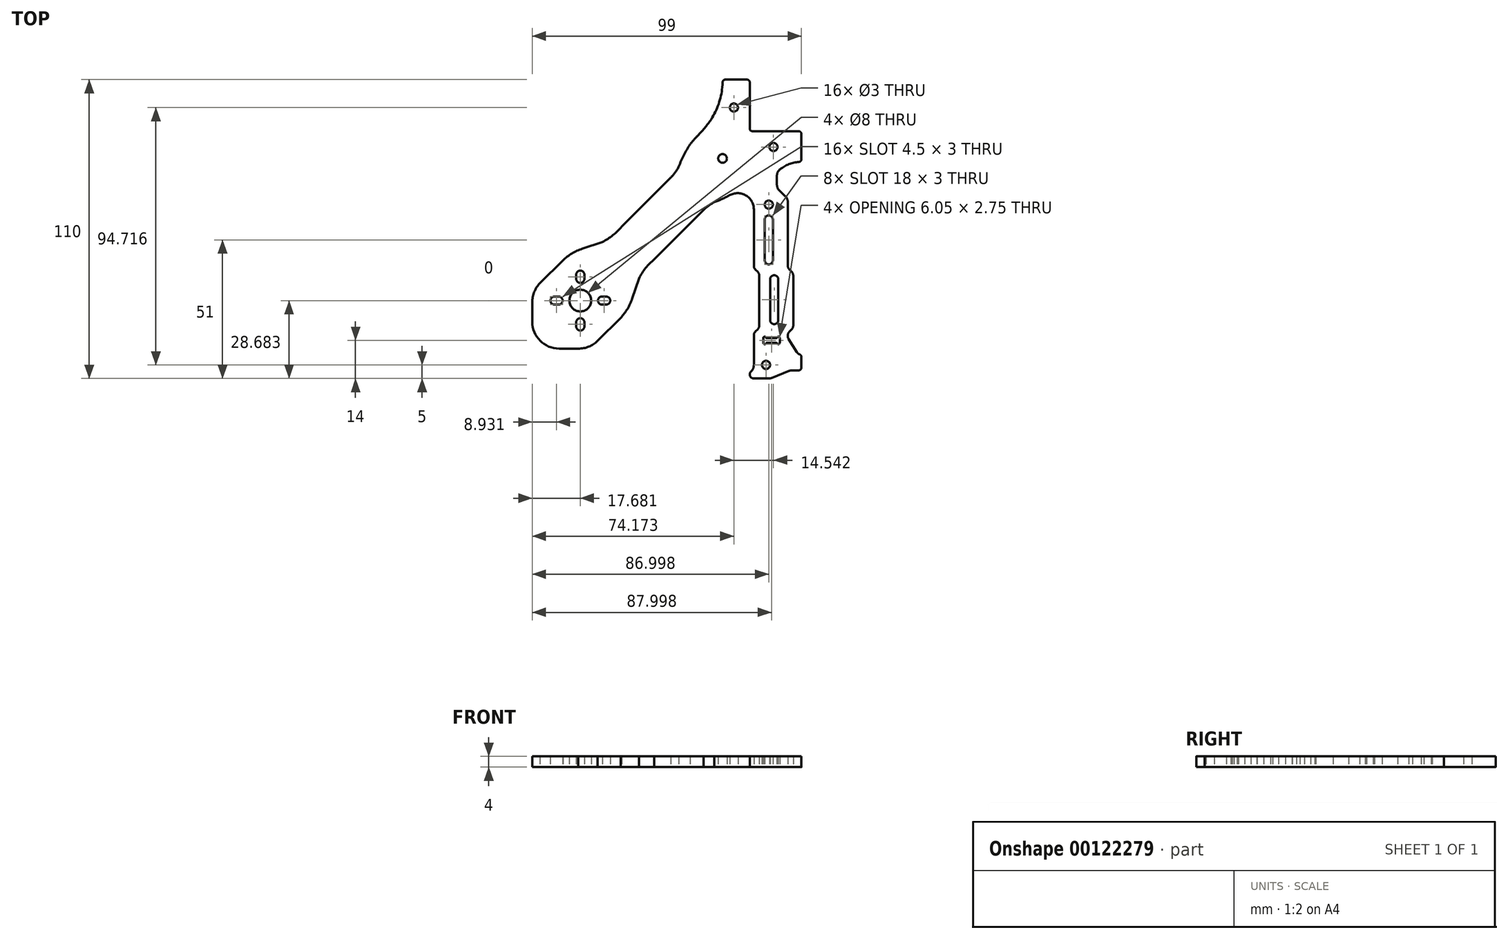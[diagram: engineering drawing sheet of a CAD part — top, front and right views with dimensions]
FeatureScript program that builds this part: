
annotation { "Feature Type Name" : "Feature", "Feature Type Description" : "" }
export const myFeature = defineFeature(function(context is Context, id is Id, definition is map)
    precondition{}
    {
        {
            var Q0;
            Q0=qCreatedBy(makeId("Top.planeOp"),FACE);
            var sketch = newSketch(context, id + "F0", { "sketchPlane" : qUnion([Q0])});
            skLineSegment(sketch, "E0", {"start": v(32, -55) * mm, "end": v(37.42, -55) * mm});
            skArc(sketch, "E1", {"start": v(31, -52.38) * mm, "mid": v(30.6, -54.04) * mm, "end": v(32, -55) * mm});
            skLineSegment(sketch, "E2", {"start": v(44.96, -52.21) * mm, "end": v(38.53, -54.79) * mm});
            skArc(sketch, "E3", {"start": v(31, -52.38) * mm, "mid": v(31.74, -51.37) * mm, "end": v(32, -50.15) * mm});
            skArc(sketch, "E4", {"start": v(37.42, -55) * mm, "mid": v(37.99, -54.95) * mm, "end": v(38.53, -54.79) * mm});
            skArc(sketch, "E5", {"start": v(46.08, -52) * mm, "mid": v(45.5, -52.05) * mm, "end": v(44.96, -52.21) * mm});
            skCircle(sketch, "E6", {"center": v(37.5, 9) * mm, "radius": 1.5 * mm});
            skLineSegment(sketch, "E7", {"start": v(46.08, -52) * mm, "end": v(48.5, -52) * mm});
            skArc(sketch, "E8", {"start": v(48.5, -52) * mm, "mid": v(49.2, -51.7) * mm, "end": v(49.5, -51) * mm});
            skLineSegment(sketch, "E9", {"start": v(33.41, -15.73) * mm, "end": v(32.58, -14.9) * mm});
            skLineSegment(sketch, "E10", {"start": v(32.58, -37.73) * mm, "end": v(33.41, -36.9) * mm});
            skLineSegment(sketch, "E11", {"start": v(32, -39.15) * mm, "end": v(32, -50.15) * mm});
            skLineSegment(sketch, "E12", {"start": v(34, -17.15) * mm, "end": v(34, -35.49) * mm});
            skArc(sketch, "E13", {"start": v(32.58, -37.73) * mm, "mid": v(32.15, -38.38) * mm, "end": v(32, -39.15) * mm});
            skArc(sketch, "E14", {"start": v(33.41, -36.9) * mm, "mid": v(33.85, -36.25) * mm, "end": v(34, -35.49) * mm});
            skArc(sketch, "E15", {"start": v(32, -13.49) * mm, "mid": v(32.15, -14.25) * mm, "end": v(32.58, -14.9) * mm});
            skArc(sketch, "E16", {"start": v(34, -17.15) * mm, "mid": v(33.85, -16.38) * mm, "end": v(33.41, -15.73) * mm});
            skCircle(sketch, "E17", {"center": v(-31.82, -26.32) * mm, "radius": 4 * mm});
            skArc(sketch, "E18", {"start": v(-41.32, -24.82) * mm, "mid": v(-42.82, -26.32) * mm, "end": v(-41.32, -27.82) * mm});
            skArc(sketch, "E19", {"start": v(-39.82, -27.82) * mm, "mid": v(-38.32, -26.32) * mm, "end": v(-39.82, -24.82) * mm});
            skArc(sketch, "E20", {"start": v(-30.32, -16.82) * mm, "mid": v(-31.82, -15.32) * mm, "end": v(-33.32, -16.82) * mm});
            skArc(sketch, "E21", {"start": v(-33.32, -18.32) * mm, "mid": v(-31.82, -19.82) * mm, "end": v(-30.32, -18.32) * mm});
            skArc(sketch, "E22", {"start": v(-23.82, -24.82) * mm, "mid": v(-25.32, -26.32) * mm, "end": v(-23.82, -27.82) * mm});
            skArc(sketch, "E23", {"start": v(-22.32, -27.82) * mm, "mid": v(-20.82, -26.32) * mm, "end": v(-22.32, -24.82) * mm});
            skArc(sketch, "E24", {"start": v(-30.32, -34.32) * mm, "mid": v(-31.82, -32.82) * mm, "end": v(-33.32, -34.32) * mm});
            skArc(sketch, "E25", {"start": v(-33.32, -35.82) * mm, "mid": v(-31.82, -37.32) * mm, "end": v(-30.32, -35.82) * mm});
            skLineSegment(sketch, "E26", {"start": v(-41.32, -24.82) * mm, "end": v(-39.82, -24.82) * mm});
            skLineSegment(sketch, "E27", {"start": v(-39.82, -27.82) * mm, "end": v(-41.32, -27.82) * mm});
            skLineSegment(sketch, "E28", {"start": v(-33.32, -16.82) * mm, "end": v(-33.32, -18.32) * mm});
            skLineSegment(sketch, "E29", {"start": v(-30.32, -16.82) * mm, "end": v(-30.32, -18.32) * mm});
            skLineSegment(sketch, "E30", {"start": v(-22.32, -24.82) * mm, "end": v(-23.82, -24.82) * mm});
            skLineSegment(sketch, "E31", {"start": v(-22.32, -27.82) * mm, "end": v(-23.82, -27.82) * mm});
            skLineSegment(sketch, "E32", {"start": v(-30.32, -34.32) * mm, "end": v(-30.32, -35.82) * mm});
            skLineSegment(sketch, "E33", {"start": v(-33.32, -34.32) * mm, "end": v(-33.32, -35.82) * mm});
            skLineSegment(sketch, "E34", {"start": v(-25.46, -41.17) * mm, "end": v(-16.97, -32.68) * mm});
            skLineSegment(sketch, "E35", {"start": v(-38.18, -11.47) * mm, "end": v(-46.67, -19.95) * mm});
            skArc(sketch, "E36", {"start": v(-49.5, -34.1) * mm, "mid": v(-46.6, -41.1) * mm, "end": v(-39.6, -44) * mm});
            skLineSegment(sketch, "E37", {"start": v(-49.5, -34.1) * mm, "end": v(-49.5, -27.02) * mm});
            skLineSegment(sketch, "E38", {"start": v(-39.6, -44) * mm, "end": v(-32.53, -44) * mm});
            skLineSegment(sketch, "E39", {"start": v(-12.73, -25.61) * mm, "end": v(-10.25, -18.19) * mm});
            skLineSegment(sketch, "E40", {"start": v(-31.11, -7.23) * mm, "end": v(-23.69, -4.75) * mm});
            skArc(sketch, "E41", {"start": v(-23.69, -4.75) * mm, "mid": v(-19.85, -2.3) * mm, "end": v(-16.62, 0.9) * mm});
            skArc(sketch, "E42", {"start": v(-4.6, -11.11) * mm, "mid": v(-7.8, -14.35) * mm, "end": v(-10.25, -18.19) * mm});
            skArc(sketch, "E43", {"start": v(-16.97, -32.68) * mm, "mid": v(-14.48, -29.37) * mm, "end": v(-12.73, -25.61) * mm});
            skArc(sketch, "E44", {"start": v(-31.11, -7.23) * mm, "mid": v(-34.87, -8.98) * mm, "end": v(-38.18, -11.47) * mm});
            skArc(sketch, "E45", {"start": v(-46.67, -19.95) * mm, "mid": v(-48.79, -23.2) * mm, "end": v(-49.5, -27.02) * mm});
            skArc(sketch, "E46", {"start": v(-32.53, -44) * mm, "mid": v(-28.7, -43.28) * mm, "end": v(-25.46, -41.17) * mm});
            skLineSegment(sketch, "E47", {"start": v(1.41, 18.94) * mm, "end": v(-16.62, 0.9) * mm});
            skLineSegment(sketch, "E48", {"start": v(32, 7.22) * mm, "end": v(32, -13.49) * mm});
            skArc(sketch, "E49", {"start": v(17.5, 9.92) * mm, "mid": v(15.37, 8.64) * mm, "end": v(13.5, 7) * mm});
            skArc(sketch, "E50", {"start": v(1.41, 18.94) * mm, "mid": v(3.1, 20.84) * mm, "end": v(4.42, 23) * mm});
            skLineSegment(sketch, "E51", {"start": v(46.5, -17.15) * mm, "end": v(46.5, -35.49) * mm});
            skLineSegment(sketch, "E52", {"start": v(45.08, -37.73) * mm, "end": v(45.91, -36.9) * mm});
            skLineSegment(sketch, "E53", {"start": v(45.91, -15.73) * mm, "end": v(45.08, -14.9) * mm});
            skLineSegment(sketch, "E54", {"start": v(44.5, -13.49) * mm, "end": v(44.5, 9.96) * mm});
            skLineSegment(sketch, "E55", {"start": v(44.5, -39.43) * mm, "end": v(44.5, -39.15) * mm});
            skArc(sketch, "E56", {"start": v(44.5, -13.49) * mm, "mid": v(44.65, -14.25) * mm, "end": v(45.08, -14.9) * mm});
            skArc(sketch, "E57", {"start": v(46.5, -17.15) * mm, "mid": v(46.35, -16.38) * mm, "end": v(45.91, -15.73) * mm});
            skArc(sketch, "E58", {"start": v(45.08, -37.73) * mm, "mid": v(44.65, -38.38) * mm, "end": v(44.5, -39.15) * mm});
            skArc(sketch, "E59", {"start": v(45.91, -36.9) * mm, "mid": v(46.35, -36.25) * mm, "end": v(46.5, -35.49) * mm});
            skLineSegment(sketch, "E60", {"start": v(41, -33.5) * mm, "end": v(41, -18.5) * mm});
            skLineSegment(sketch, "E61", {"start": v(38, -18.5) * mm, "end": v(38, -33.5) * mm});
            skArc(sketch, "E62", {"start": v(38, -33.5) * mm, "mid": v(39.5, -35) * mm, "end": v(41, -33.5) * mm});
            skArc(sketch, "E63", {"start": v(41, -18.5) * mm, "mid": v(39.5, -17) * mm, "end": v(38, -18.5) * mm});
            skLineSegment(sketch, "E64", {"start": v(39, -11.5) * mm, "end": v(39, 3.5) * mm});
            skLineSegment(sketch, "E65", {"start": v(36, 3.5) * mm, "end": v(36, -11.5) * mm});
            skArc(sketch, "E66", {"start": v(36, -11.5) * mm, "mid": v(37.5, -13) * mm, "end": v(39, -11.5) * mm});
            skArc(sketch, "E67", {"start": v(39, 3.5) * mm, "mid": v(37.5, 5) * mm, "end": v(36, 3.5) * mm});
            skCircle(sketch, "E68", {"center": v(39.22, 30.17) * mm, "radius": 1.5 * mm});
            skCircle(sketch, "E69", {"center": v(24.67, 44.72) * mm, "radius": 1.5 * mm});
            skLineSegment(sketch, "E70", {"start": v(44.8, -40.49) * mm, "end": v(47.8, -45.29) * mm});
            skArc(sketch, "E71", {"start": v(44.5, -39.43) * mm, "mid": v(44.58, -39.98) * mm, "end": v(44.8, -40.49) * mm});
            skLineSegment(sketch, "E72", {"start": v(49.5, -47.05) * mm, "end": v(49.5, -51) * mm});
            skArc(sketch, "E73", {"start": v(47.8, -45.29) * mm, "mid": v(48.25, -45.79) * mm, "end": v(48.83, -46.11) * mm});
            skArc(sketch, "E74", {"start": v(49.5, -47.05) * mm, "mid": v(49.31, -46.48) * mm, "end": v(48.83, -46.11) * mm});
            skLineSegment(sketch, "E75", {"start": v(-4.6, -11.11) * mm, "end": v(13.5, 7) * mm});
            skArc(sketch, "E76", {"start": v(30.5, 37) * mm, "mid": v(30.8, 36.3) * mm, "end": v(31.5, 36) * mm});
            skLineSegment(sketch, "E77", {"start": v(31.5, 36) * mm, "end": v(48.5, 36) * mm});
            skArc(sketch, "E78", {"start": v(49.5, 35) * mm, "mid": v(49.2, 35.7) * mm, "end": v(48.5, 36) * mm});
            skLineSegment(sketch, "E79", {"start": v(30.5, 54) * mm, "end": v(30.5, 37) * mm});
            skArc(sketch, "E80", {"start": v(30.5, 54) * mm, "mid": v(30.2, 54.7) * mm, "end": v(29.5, 55) * mm});
            skCircle(sketch, "E81", {"center": v(36.5, -50) * mm, "radius": 1.5 * mm});
            skCircle(sketch, "E82", {"center": v(20.5, 26) * mm, "radius": 1.6 * mm});
            skArc(sketch, "E83", {"start": v(16.27, 40.35) * mm, "mid": v(19.05, 46) * mm, "end": v(20.4, 52.17) * mm});
            skArc(sketch, "E84", {"start": v(11.73, 34.76) * mm, "mid": v(14.15, 37.44) * mm, "end": v(16.27, 40.35) * mm});
            skArc(sketch, "E85", {"start": v(11.73, 34.76) * mm, "mid": v(10.12, 33.04) * mm, "end": v(8.61, 31.23) * mm});
            skArc(sketch, "E86", {"start": v(8.61, 31.23) * mm, "mid": v(6.25, 27.25) * mm, "end": v(4.42, 23) * mm});
            skArc(sketch, "E87", {"start": v(17.5, 9.92) * mm, "mid": v(20.33, 11.06) * mm, "end": v(23.05, 12.45) * mm});
            skArc(sketch, "E88", {"start": v(20.4, 52.17) * mm, "mid": v(20.47, 53.1) * mm, "end": v(20.51, 54.03) * mm});
            skArc(sketch, "E89", {"start": v(21.51, 55) * mm, "mid": v(20.82, 54.72) * mm, "end": v(20.51, 54.03) * mm});
            skLineSegment(sketch, "E90", {"start": v(21.51, 55) * mm, "end": v(29.5, 55) * mm});
            skLineSegment(sketch, "E91", {"start": v(40.5, 19.66) * mm, "end": v(40.5, 16.3) * mm});
            skLineSegment(sketch, "E92", {"start": v(41.45, 14.11) * mm, "end": v(43.54, 12.16) * mm});
            skArc(sketch, "E93", {"start": v(48.57, 24.7) * mm, "mid": v(44.9, 23.87) * mm, "end": v(41.65, 22.02) * mm});
            skArc(sketch, "E94", {"start": v(48.57, 24.7) * mm, "mid": v(49.23, 25.01) * mm, "end": v(49.5, 25.7) * mm});
            skLineSegment(sketch, "E95", {"start": v(49.5, 35) * mm, "end": v(49.5, 25.7) * mm});
            skArc(sketch, "E96", {"start": v(44.5, 9.96) * mm, "mid": v(44.25, 11.16) * mm, "end": v(43.54, 12.16) * mm});
            skArc(sketch, "E97", {"start": v(40.5, 16.3) * mm, "mid": v(40.75, 15.1) * mm, "end": v(41.45, 14.11) * mm});
            skArc(sketch, "E98", {"start": v(41.65, 22.02) * mm, "mid": v(40.8, 20.97) * mm, "end": v(40.5, 19.66) * mm});
            skArc(sketch, "E99", {"start": v(32, 7.22) * mm, "mid": v(29.03, 12.4) * mm, "end": v(23.05, 12.45) * mm});
            skLineSegment(sketch, "E100", {"start": v(41.52, -41.88) * mm, "end": v(41.52, -40.12) * mm});
            skLineSegment(sketch, "E101", {"start": v(35.47, -40.12) * mm, "end": v(35.47, -41.88) * mm});
            skArc(sketch, "E102", {"start": v(36.4, -39.88) * mm, "mid": v(35.84, -39.64) * mm, "end": v(35.47, -40.12) * mm});
            skArc(sketch, "E103", {"start": v(35.47, -41.88) * mm, "mid": v(35.84, -42.36) * mm, "end": v(36.4, -42.12) * mm});
            skArc(sketch, "E104", {"start": v(40.59, -42.12) * mm, "mid": v(41.15, -42.36) * mm, "end": v(41.52, -41.88) * mm});
            skArc(sketch, "E105", {"start": v(41.52, -40.12) * mm, "mid": v(41.15, -39.64) * mm, "end": v(40.59, -39.88) * mm});
            skLineSegment(sketch, "E106", {"start": v(36.84, -40.12) * mm, "end": v(40.16, -40.12) * mm});
            skLineSegment(sketch, "E107", {"start": v(40.16, -41.88) * mm, "end": v(36.84, -41.88) * mm});
            skArc(sketch, "E108", {"start": v(36.4, -39.88) * mm, "mid": v(36.59, -40.06) * mm, "end": v(36.84, -40.12) * mm});
            skArc(sketch, "E109", {"start": v(40.16, -40.12) * mm, "mid": v(40.4, -40.06) * mm, "end": v(40.59, -39.88) * mm});
            skArc(sketch, "E110", {"start": v(40.59, -42.12) * mm, "mid": v(40.4, -41.94) * mm, "end": v(40.16, -41.88) * mm});
            skArc(sketch, "E111", {"start": v(36.84, -41.88) * mm, "mid": v(36.59, -41.94) * mm, "end": v(36.4, -42.12) * mm});
            skSolve(sketch);
        }
        {
            var Q0;
            Q0 = qSketchRegion(id + "F0", true);
            extrude(context, id + "F1", {"entities" : qUnion([Q0]), "depth" : 4 * mm});
        }
    });
